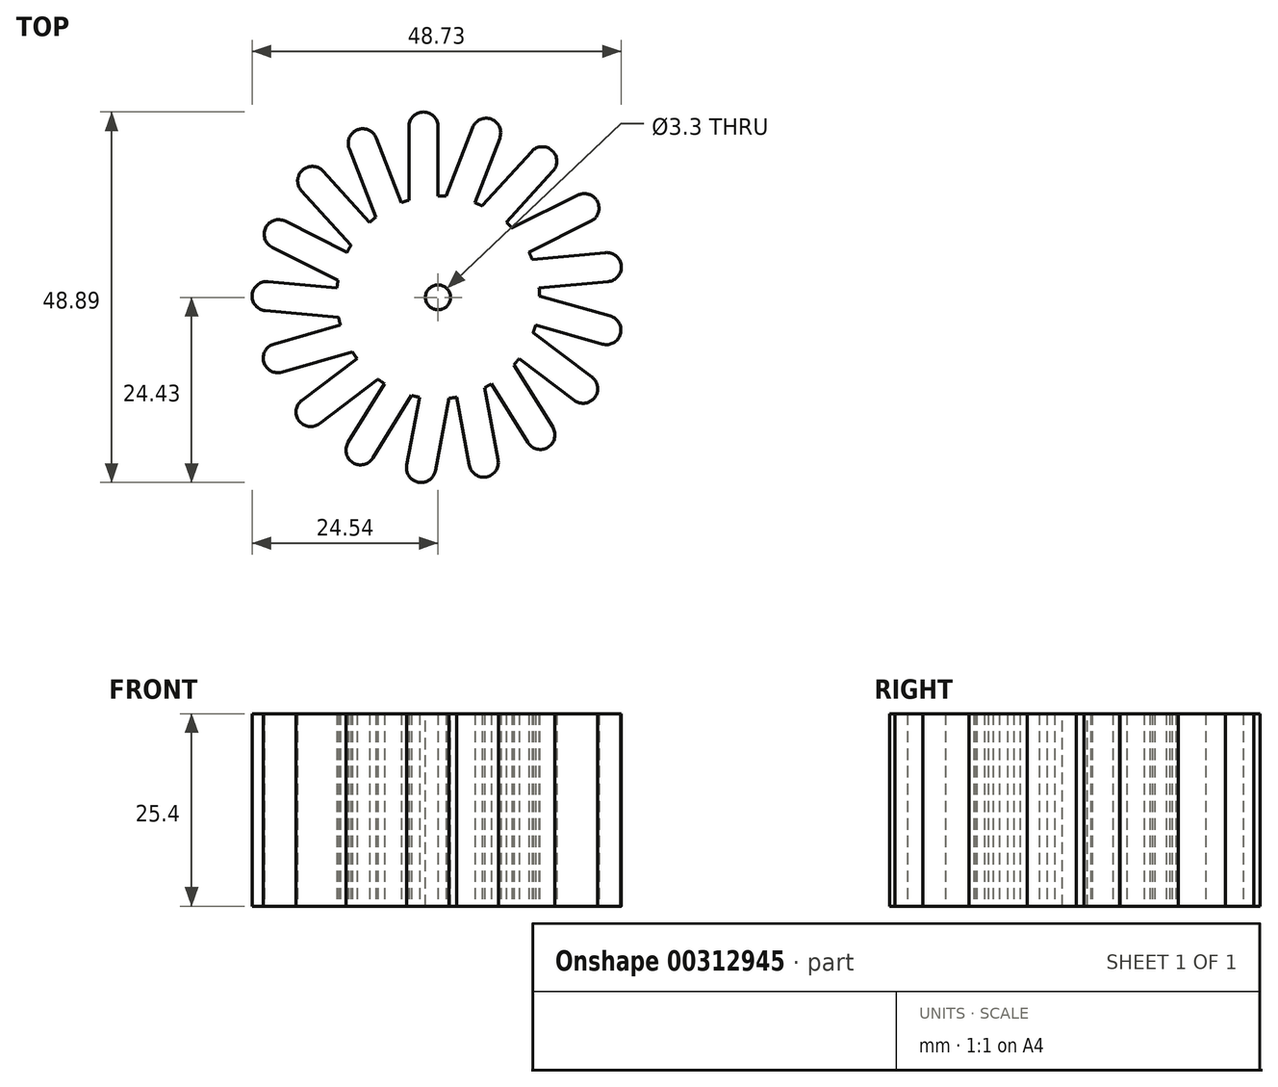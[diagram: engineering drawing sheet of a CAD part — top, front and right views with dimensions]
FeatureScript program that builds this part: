
annotation { "Feature Type Name" : "Feature", "Feature Type Description" : "" }
export const myFeature = defineFeature(function(context is Context, id is Id, definition is map)
    precondition{}
    {
        {
            var Q0;
            Q0=qCreatedBy(makeId("Top.planeOp"),FACE);
            var sketch = newSketch(context, id + "F0", { "sketchPlane" : qUnion([Q0])});
            skCircle(sketch, "E0", {"center": v(0, 0) * mm, "radius": 13.4 * mm});
            skLineSegment(sketch, "E1", {"start": v(-3.85, 12.83) * mm, "end": v(-3.85, 22.54) * mm});
            skArc(sketch, "E2", {"start": v(0, 22.54) * mm, "mid": v(-1.92, 24.46) * mm, "end": v(-3.85, 22.54) * mm});
            skLineSegment(sketch, "E3", {"start": v(0, 22.54) * mm, "end": v(0, 13.4) * mm});
            skLineSegment(sketch, "E4.1.0", {"start": v(-8.22, 10.58) * mm, "end": v(-11.73, 19.63) * mm});
            skArc(sketch, "E4.1.1", {"start": v(-8.14, 21.02) * mm, "mid": v(-10.63, 22.11) * mm, "end": v(-11.73, 19.63) * mm});
            skLineSegment(sketch, "E4.1.2", {"start": v(-8.14, 21.02) * mm, "end": v(-4.84, 12.5) * mm});
            skLineSegment(sketch, "E4.2.0", {"start": v(-11.49, 6.9) * mm, "end": v(-18.03, 14.06) * mm});
            skArc(sketch, "E4.2.1", {"start": v(-15.18, 16.66) * mm, "mid": v(-17.9, 16.78) * mm, "end": v(-18.03, 14.06) * mm});
            skLineSegment(sketch, "E4.2.2", {"start": v(-15.18, 16.66) * mm, "end": v(-9.03, 9.9) * mm});
            skLineSegment(sketch, "E4.3.0", {"start": v(-13.2, 2.28) * mm, "end": v(-21.89, 6.6) * mm});
            skArc(sketch, "E4.3.1", {"start": v(-20.17, 10.05) * mm, "mid": v(-22.75, 9.18) * mm, "end": v(-21.89, 6.6) * mm});
            skLineSegment(sketch, "E4.3.2", {"start": v(-20.17, 10.05) * mm, "end": v(-12, 5.97) * mm});
            skLineSegment(sketch, "E4.4.0", {"start": v(-13.13, -2.65) * mm, "end": v(-22.8, -1.75) * mm});
            skArc(sketch, "E4.4.1", {"start": v(-22.44, 2.08) * mm, "mid": v(-24.53, 0.34) * mm, "end": v(-22.8, -1.75) * mm});
            skLineSegment(sketch, "E4.4.2", {"start": v(-22.44, 2.08) * mm, "end": v(-13.34, 1.24) * mm});
            skLineSegment(sketch, "E5.1.5.0", {"start": v(-11.3, -7.21) * mm, "end": v(-20.62, -9.87) * mm});
            skArc(sketch, "E5.3.5.0", {"start": v(-21.68, -6.17) * mm, "mid": v(-23, -8.54) * mm, "end": v(-20.62, -9.87) * mm});
            skLineSegment(sketch, "E5.7.5.0", {"start": v(-21.68, -6.17) * mm, "end": v(-12.89, -3.67) * mm});
            skLineSegment(sketch, "E5.1.6.0", {"start": v(-7.92, -10.8) * mm, "end": v(-15.67, -16.65) * mm});
            skArc(sketch, "E5.3.6.0", {"start": v(-17.99, -13.58) * mm, "mid": v(-18.36, -16.28) * mm, "end": v(-15.67, -16.65) * mm});
            skLineSegment(sketch, "E5.7.6.0", {"start": v(-17.99, -13.58) * mm, "end": v(-10.7, -8.07) * mm});
            skLineSegment(sketch, "E5.1.7.0", {"start": v(-3.48, -12.94) * mm, "end": v(-8.6, -21.19) * mm});
            skArc(sketch, "E5.3.7.0", {"start": v(-11.86, -19.16) * mm, "mid": v(-11.24, -21.81) * mm, "end": v(-8.6, -21.19) * mm});
            skLineSegment(sketch, "E5.7.7.0", {"start": v(-11.86, -19.16) * mm, "end": v(-7.05, -11.4) * mm});
            skLineSegment(sketch, "E5.1.8.0", {"start": v(1.42, -13.32) * mm, "end": v(-0.36, -22.86) * mm});
            skArc(sketch, "E5.3.8.0", {"start": v(-4.14, -22.15) * mm, "mid": v(-2.6, -24.4) * mm, "end": v(-0.36, -22.86) * mm});
            skLineSegment(sketch, "E5.7.8.0", {"start": v(-4.14, -22.15) * mm, "end": v(-2.46, -13.17) * mm});
            skLineSegment(sketch, "E5.1.9.0", {"start": v(6.14, -11.9) * mm, "end": v(7.92, -21.45) * mm});
            skArc(sketch, "E5.3.9.0", {"start": v(4.14, -22.15) * mm, "mid": v(6.39, -23.7) * mm, "end": v(7.92, -21.45) * mm});
            skLineSegment(sketch, "E5.7.9.0", {"start": v(4.14, -22.15) * mm, "end": v(2.46, -13.17) * mm});
            skLineSegment(sketch, "E5.1.10.0", {"start": v(10.03, -8.89) * mm, "end": v(15.14, -17.14) * mm});
            skArc(sketch, "E5.3.10.0", {"start": v(11.86, -19.16) * mm, "mid": v(14.51, -19.78) * mm, "end": v(15.14, -17.14) * mm});
            skLineSegment(sketch, "E5.7.10.0", {"start": v(11.86, -19.16) * mm, "end": v(7.05, -11.4) * mm});
            skLineSegment(sketch, "E5.1.11.0", {"start": v(12.56, -4.66) * mm, "end": v(20.3, -10.51) * mm});
            skArc(sketch, "E5.3.11.0", {"start": v(17.99, -13.58) * mm, "mid": v(20.68, -13.2) * mm, "end": v(20.3, -10.51) * mm});
            skLineSegment(sketch, "E5.7.11.0", {"start": v(17.99, -13.58) * mm, "end": v(10.7, -8.07) * mm});
            skLineSegment(sketch, "E5.1.12.0", {"start": v(13.4, 0.19) * mm, "end": v(22.73, -2.47) * mm});
            skArc(sketch, "E5.3.12.0", {"start": v(21.68, -6.17) * mm, "mid": v(24.05, -4.84) * mm, "end": v(22.73, -2.47) * mm});
            skLineSegment(sketch, "E5.7.12.0", {"start": v(21.68, -6.17) * mm, "end": v(12.89, -3.67) * mm});
            skLineSegment(sketch, "E5.1.13.0", {"start": v(12.42, 5.02) * mm, "end": v(22.09, 5.91) * mm});
            skArc(sketch, "E5.3.13.0", {"start": v(22.44, 2.08) * mm, "mid": v(24.18, 4.17) * mm, "end": v(22.09, 5.91) * mm});
            skLineSegment(sketch, "E5.7.13.0", {"start": v(22.44, 2.08) * mm, "end": v(13.34, 1.24) * mm});
            skLineSegment(sketch, "E5.1.14.0", {"start": v(9.77, 9.16) * mm, "end": v(18.46, 13.5) * mm});
            skArc(sketch, "E5.3.14.0", {"start": v(20.17, 10.05) * mm, "mid": v(21.04, 12.63) * mm, "end": v(18.46, 13.5) * mm});
            skLineSegment(sketch, "E5.7.14.0", {"start": v(20.17, 10.05) * mm, "end": v(12, 5.97) * mm});
            skLineSegment(sketch, "E5.1.15.0", {"start": v(5.8, 12.08) * mm, "end": v(12.34, 19.25) * mm});
            skArc(sketch, "E5.3.15.0", {"start": v(15.18, 16.66) * mm, "mid": v(15.06, 19.37) * mm, "end": v(12.34, 19.25) * mm});
            skLineSegment(sketch, "E5.7.15.0", {"start": v(15.18, 16.66) * mm, "end": v(9.03, 9.9) * mm});
            skLineSegment(sketch, "E5.1.16.0", {"start": v(1.05, 13.36) * mm, "end": v(4.55, 22.4) * mm});
            skArc(sketch, "E5.3.16.0", {"start": v(8.14, 21.02) * mm, "mid": v(7.04, 23.5) * mm, "end": v(4.55, 22.4) * mm});
            skLineSegment(sketch, "E5.7.16.0", {"start": v(8.14, 21.02) * mm, "end": v(4.84, 12.5) * mm});
            skSolve(sketch);
        }
        {
            var Q0;
            {var subQ0=sQuery(id+"F0.wireOp",EDGE,"E0");var subQ18=makeQuery(id+"F0.imprint","INTERSECT",VERTEX,{"derivedFrom":[subQ0,sQuery(id+"F0.wireOp",EDGE,"E5.1.12.0")]});Q0=makeQuery(id+"F0.imprint","IMPRINT",FACE,{"disambiguationData":[TD([[makeQuery(id+"F0.imprint","IMPRINT",EDGE,{"disambiguationData":[TD([[subQ18,-1.0]])],"derivedFrom":subQ0}),1.0]])]});}
            var Q1;
            {var subQ0=sQuery(id+"F0.wireOp",EDGE,"E5.1.10.0");Q1=makeQuery(id+"F0.imprint","IMPRINT",FACE,{"disambiguationData":[TD([[makeQuery(id+"F0.imprint","IMPRINT",EDGE,{"derivedFrom":subQ0}),-1.0]])]});}
            var Q2;
            {var subQ0=sQuery(id+"F0.wireOp",EDGE,"E5.1.11.0");Q2=makeQuery(id+"F0.imprint","IMPRINT",FACE,{"disambiguationData":[TD([[makeQuery(id+"F0.imprint","IMPRINT",EDGE,{"derivedFrom":subQ0}),-1.0]])]});}
            var Q3;
            {var subQ0=sQuery(id+"F0.wireOp",EDGE,"E5.1.12.0");Q3=makeQuery(id+"F0.imprint","IMPRINT",FACE,{"disambiguationData":[TD([[makeQuery(id+"F0.imprint","IMPRINT",EDGE,{"derivedFrom":subQ0}),-1.0]])]});}
            var Q4;
            {var subQ0=sQuery(id+"F0.wireOp",EDGE,"E5.1.13.0");Q4=makeQuery(id+"F0.imprint","IMPRINT",FACE,{"disambiguationData":[TD([[makeQuery(id+"F0.imprint","IMPRINT",EDGE,{"derivedFrom":subQ0}),-1.0]])]});}
            var Q5;
            {var subQ0=sQuery(id+"F0.wireOp",EDGE,"E5.1.14.0");Q5=makeQuery(id+"F0.imprint","IMPRINT",FACE,{"disambiguationData":[TD([[makeQuery(id+"F0.imprint","IMPRINT",EDGE,{"derivedFrom":subQ0}),-1.0]])]});}
            var Q6;
            {var subQ0=sQuery(id+"F0.wireOp",EDGE,"E5.1.15.0");Q6=makeQuery(id+"F0.imprint","IMPRINT",FACE,{"disambiguationData":[TD([[makeQuery(id+"F0.imprint","IMPRINT",EDGE,{"derivedFrom":subQ0}),-1.0]])]});}
            var Q7;
            {var subQ0=sQuery(id+"F0.wireOp",EDGE,"E5.1.16.0");Q7=makeQuery(id+"F0.imprint","IMPRINT",FACE,{"disambiguationData":[TD([[makeQuery(id+"F0.imprint","IMPRINT",EDGE,{"derivedFrom":subQ0}),-1.0]])]});}
            var Q8;
            {var subQ0=sQuery(id+"F0.wireOp",EDGE,"E1");Q8=makeQuery(id+"F0.imprint","IMPRINT",FACE,{"disambiguationData":[TD([[makeQuery(id+"F0.imprint","IMPRINT",EDGE,{"derivedFrom":subQ0}),-1.0]])]});}
            var Q9;
            {var subQ0=sQuery(id+"F0.wireOp",EDGE,"E4.1.0");Q9=makeQuery(id+"F0.imprint","IMPRINT",FACE,{"disambiguationData":[TD([[makeQuery(id+"F0.imprint","IMPRINT",EDGE,{"derivedFrom":subQ0}),-1.0]])]});}
            var Q10;
            {var subQ0=sQuery(id+"F0.wireOp",EDGE,"E4.2.0");Q10=makeQuery(id+"F0.imprint","IMPRINT",FACE,{"disambiguationData":[TD([[makeQuery(id+"F0.imprint","IMPRINT",EDGE,{"derivedFrom":subQ0}),-1.0]])]});}
            var Q11;
            {var subQ0=sQuery(id+"F0.wireOp",EDGE,"E4.3.0");Q11=makeQuery(id+"F0.imprint","IMPRINT",FACE,{"disambiguationData":[TD([[makeQuery(id+"F0.imprint","IMPRINT",EDGE,{"derivedFrom":subQ0}),-1.0]])]});}
            var Q12;
            {var subQ0=sQuery(id+"F0.wireOp",EDGE,"E4.4.0");Q12=makeQuery(id+"F0.imprint","IMPRINT",FACE,{"disambiguationData":[TD([[makeQuery(id+"F0.imprint","IMPRINT",EDGE,{"derivedFrom":subQ0}),-1.0]])]});}
            var Q13;
            {var subQ0=sQuery(id+"F0.wireOp",EDGE,"E5.1.5.0");Q13=makeQuery(id+"F0.imprint","IMPRINT",FACE,{"disambiguationData":[TD([[makeQuery(id+"F0.imprint","IMPRINT",EDGE,{"derivedFrom":subQ0}),-1.0]])]});}
            var Q14;
            {var subQ0=sQuery(id+"F0.wireOp",EDGE,"E5.1.6.0");Q14=makeQuery(id+"F0.imprint","IMPRINT",FACE,{"disambiguationData":[TD([[makeQuery(id+"F0.imprint","IMPRINT",EDGE,{"derivedFrom":subQ0}),-1.0]])]});}
            var Q15;
            {var subQ0=sQuery(id+"F0.wireOp",EDGE,"E5.1.7.0");Q15=makeQuery(id+"F0.imprint","IMPRINT",FACE,{"disambiguationData":[TD([[makeQuery(id+"F0.imprint","IMPRINT",EDGE,{"derivedFrom":subQ0}),-1.0]])]});}
            var Q16;
            {var subQ0=sQuery(id+"F0.wireOp",EDGE,"E5.1.8.0");Q16=makeQuery(id+"F0.imprint","IMPRINT",FACE,{"disambiguationData":[TD([[makeQuery(id+"F0.imprint","IMPRINT",EDGE,{"derivedFrom":subQ0}),-1.0]])]});}
            var Q17;
            {var subQ0=sQuery(id+"F0.wireOp",EDGE,"E5.1.9.0");Q17=makeQuery(id+"F0.imprint","IMPRINT",FACE,{"disambiguationData":[TD([[makeQuery(id+"F0.imprint","IMPRINT",EDGE,{"derivedFrom":subQ0}),-1.0]])]});}
            extrude(context, id + "F1", {"entities" : qUnion([Q0, Q1, Q2, Q3, Q4, Q5, Q6, Q7, Q8, Q9, Q10, Q11, Q12, Q13, Q14, Q15, Q16, Q17]), "depth" : 25.4 * mm});
        }
        {
            var Q0;
            Q0=makeQuery(id+"F1.opExtrude","CAP_FACE",FACE,{"disambiguationData":[OSD([sQuery(id+"F0.wireOp",EDGE,"E0"),sQuery(id+"F0.wireOp",EDGE,"E1"),sQuery(id+"F0.wireOp",EDGE,"E2"),sQuery(id+"F0.wireOp",EDGE,"E3"),sQuery(id+"F0.wireOp",EDGE,"E4.1.0"),sQuery(id+"F0.wireOp",EDGE,"E4.1.1"),sQuery(id+"F0.wireOp",EDGE,"E4.1.2"),sQuery(id+"F0.wireOp",EDGE,"E4.2.0"),sQuery(id+"F0.wireOp",EDGE,"E4.2.1"),sQuery(id+"F0.wireOp",EDGE,"E4.2.2"),sQuery(id+"F0.wireOp",EDGE,"E4.3.0"),sQuery(id+"F0.wireOp",EDGE,"E4.3.1"),sQuery(id+"F0.wireOp",EDGE,"E4.3.2"),sQuery(id+"F0.wireOp",EDGE,"E4.4.0"),sQuery(id+"F0.wireOp",EDGE,"E4.4.1"),sQuery(id+"F0.wireOp",EDGE,"E4.4.2"),sQuery(id+"F0.wireOp",EDGE,"E5.1.5.0"),sQuery(id+"F0.wireOp",EDGE,"E5.3.5.0"),sQuery(id+"F0.wireOp",EDGE,"E5.7.5.0"),sQuery(id+"F0.wireOp",EDGE,"E5.1.6.0"),sQuery(id+"F0.wireOp",EDGE,"E5.3.6.0"),sQuery(id+"F0.wireOp",EDGE,"E5.7.6.0"),sQuery(id+"F0.wireOp",EDGE,"E5.1.7.0"),sQuery(id+"F0.wireOp",EDGE,"E5.3.7.0"),sQuery(id+"F0.wireOp",EDGE,"E5.7.7.0"),sQuery(id+"F0.wireOp",EDGE,"E5.1.8.0"),sQuery(id+"F0.wireOp",EDGE,"E5.3.8.0"),sQuery(id+"F0.wireOp",EDGE,"E5.7.8.0"),sQuery(id+"F0.wireOp",EDGE,"E5.1.9.0"),sQuery(id+"F0.wireOp",EDGE,"E5.3.9.0"),sQuery(id+"F0.wireOp",EDGE,"E5.7.9.0"),sQuery(id+"F0.wireOp",EDGE,"E5.1.10.0"),sQuery(id+"F0.wireOp",EDGE,"E5.3.10.0"),sQuery(id+"F0.wireOp",EDGE,"E5.7.10.0"),sQuery(id+"F0.wireOp",EDGE,"E5.1.11.0"),sQuery(id+"F0.wireOp",EDGE,"E5.3.11.0"),sQuery(id+"F0.wireOp",EDGE,"E5.7.11.0"),sQuery(id+"F0.wireOp",EDGE,"E5.1.12.0"),sQuery(id+"F0.wireOp",EDGE,"E5.3.12.0"),sQuery(id+"F0.wireOp",EDGE,"E5.7.12.0"),sQuery(id+"F0.wireOp",EDGE,"E5.1.13.0"),sQuery(id+"F0.wireOp",EDGE,"E5.3.13.0"),sQuery(id+"F0.wireOp",EDGE,"E5.7.13.0"),sQuery(id+"F0.wireOp",EDGE,"E5.1.14.0"),sQuery(id+"F0.wireOp",EDGE,"E5.3.14.0"),sQuery(id+"F0.wireOp",EDGE,"E5.7.14.0"),sQuery(id+"F0.wireOp",EDGE,"E5.1.15.0"),sQuery(id+"F0.wireOp",EDGE,"E5.3.15.0"),sQuery(id+"F0.wireOp",EDGE,"E5.7.15.0"),sQuery(id+"F0.wireOp",EDGE,"E5.1.16.0"),sQuery(id+"F0.wireOp",EDGE,"E5.3.16.0"),sQuery(id+"F0.wireOp",EDGE,"E5.7.16.0")])],"isStart":false});
            var sketch = newSketch(context, id + "F2", { "sketchPlane" : qUnion([Q0])});
            skCircle(sketch, "E6", {"center": v(0, 0) * mm, "radius": 1.65 * mm});
            skSolve(sketch);
        }
        {
            var Q0;
            Q0 = qSketchRegion(id + "F2", true);
            extrude(context, id + "F3", {"entities" : qUnion([Q0]), "operationType" : NewBodyOperationType.REMOVE, "oppositeDirection" : true, "depth" : 25.4 * mm});
        }
    });
